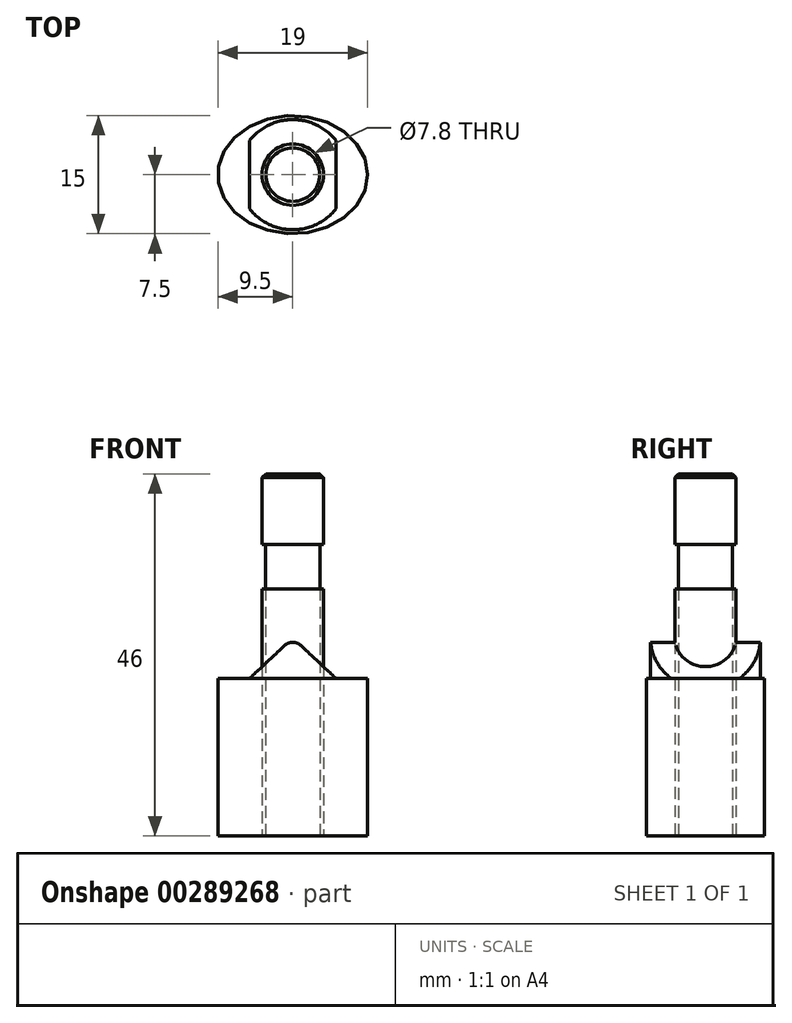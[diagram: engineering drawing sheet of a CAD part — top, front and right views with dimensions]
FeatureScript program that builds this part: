
annotation { "Feature Type Name" : "Feature", "Feature Type Description" : "" }
export const myFeature = defineFeature(function(context is Context, id is Id, definition is map)
    precondition{}
    {
        {
            var Q0;
            Q0=qCreatedBy(makeId("Top.planeOp"),FACE);
            var sketch = newSketch(context, id + "F0", { "sketchPlane" : qUnion([Q0])});
            skEllipse(sketch, "E0", {"center": v(0, 0) * mm, "majorRadius": 9.5 * mm, "minorRadius": 7.5 * mm, "majorAxis": v(1, 0)});
            skSolve(sketch);
        }
        {
            var Q0;
            Q0=makeQuery(id+"F0.imprint","IMPRINT",FACE,{"disambiguationData":[TD([[makeQuery(id+"F0.imprint","IMPRINT",EDGE,{"derivedFrom":sQuery(id+"F0.wireOp",EDGE,"E0")}),1.0]])]});
            extrude(context, id + "F1", {"entities" : qUnion([Q0]), "depth" : 20 * mm});
        }
        {
            var Q0;
            Q0=makeQuery(id+"F1.opExtrude","CAP_FACE",FACE,{"disambiguationData":[OSD([sQuery(id+"F0.wireOp",EDGE,"E0")])],"isStart":false});
            var sketch = newSketch(context, id + "F2", { "sketchPlane" : qUnion([Q0])});
            skCircle(sketch, "E1", {"center": v(0, 0) * mm, "radius": 7 * mm});
            skSolve(sketch);
        }
        {
            var Q0;
            Q0=makeQuery(id+"F2.imprint","IMPRINT",FACE,{"disambiguationData":[TD([[makeQuery(id+"F2.imprint","IMPRINT",EDGE,{"derivedFrom":sQuery(id+"F2.wireOp",EDGE,"E1")}),1.0]])]});
            extrude(context, id + "F3", {"entities" : qUnion([Q0]), "operationType" : NewBodyOperationType.ADD, "depth" : 4.6 * mm});
        }
        {
            var Q0;
            Q0=qCreatedBy(makeId("Front.planeOp"),FACE);
            var sketch = newSketch(context, id + "F4", { "sketchPlane" : qUnion([Q0])});
            skLineSegment(sketch, "E2.top", {"start": v(0, 24.6) * mm, "end": v(0, 24.6) * mm});
            skLineSegment(sketch, "E3", {"start": v(-5.5, 20) * mm, "end": v(-1.03, 24.2) * mm});
            skLineSegment(sketch, "E4", {"start": v(1.03, 24.2) * mm, "end": v(5.5, 20) * mm});
            skPoint(sketch, "E5.visualSharp", {"position": v(-0.6, 24.6) * mm});
            skArc(sketch, "E5.filletArc", {"start": v(0, 24.6) * mm, "mid": v(-0.55, 24.5) * mm, "end": v(-1.03, 24.2) * mm});
            skPoint(sketch, "E6.visualSharp", {"position": v(0.6, 24.6) * mm});
            skArc(sketch, "E6.filletArc", {"start": v(1.03, 24.2) * mm, "mid": v(0.55, 24.5) * mm, "end": v(0, 24.6) * mm});
            skLineSegment(sketch, "E7", {"start": v(-5.5, 20) * mm, "end": v(-7.13, 20) * mm});
            skLineSegment(sketch, "E8", {"start": v(-7.13, 20) * mm, "end": v(-7.13, 24.6) * mm});
            skLineSegment(sketch, "E9", {"start": v(-7.13, 24.6) * mm, "end": v(7.3, 24.6) * mm});
            skLineSegment(sketch, "E10", {"start": v(7.3, 24.6) * mm, "end": v(7.3, 20) * mm});
            skLineSegment(sketch, "E11", {"start": v(7.3, 20) * mm, "end": v(5.5, 20) * mm});
            skSolve(sketch);
        }
        {
            var Q0;
            Q0 = qSketchRegion(id + "F4", true);
            extrude(context, id + "F5", {"entities" : qUnion([Q0]), "operationType" : NewBodyOperationType.REMOVE, "endBound" : BoundingType.SYMMETRIC, "oppositeDirection" : true, "depth" : 25 * mm});
        }
        {
            var Q0;
            Q0=makeQuery(id+"F1.opExtrude","CAP_FACE",FACE,{"disambiguationData":[OSD([sQuery(id+"F0.wireOp",EDGE,"E0")])],"isStart":true});
            var sketch = newSketch(context, id + "F6", { "sketchPlane" : qUnion([Q0])});
            skCircle(sketch, "E12", {"center": v(0, 0) * mm, "radius": 3.9 * mm});
            skSolve(sketch);
        }
        {
            var Q0;
            Q0=makeQuery(id+"F6.imprint","IMPRINT",FACE,{"disambiguationData":[TD([[makeQuery(id+"F6.imprint","IMPRINT",EDGE,{"derivedFrom":sQuery(id+"F6.wireOp",EDGE,"E12")}),1.0]])]});
            extrude(context, id + "F7", {"entities" : qUnion([Q0]), "operationType" : NewBodyOperationType.REMOVE, "endBound" : BoundingType.THROUGH_ALL, "oppositeDirection" : true, "depth" : 25 * mm});
        }
        {
            var Q0;
            Q0=qCreatedBy(makeId("Top.planeOp"),FACE);
            var sketch = newSketch(context, id + "F8", { "sketchPlane" : qUnion([Q0])});
            skCircle(sketch, "E13", {"center": v(0, 0) * mm, "radius": 3.45 * mm});
            skSolve(sketch);
        }
        {
            var Q0;
            Q0 = qSketchRegion(id + "F8", true);
            extrude(context, id + "F9", {"entities" : qUnion([Q0]), "operationType" : NewBodyOperationType.ADD, "depth" : 46 * mm});
        }
        {
            var Q0;
            Q0=qCreatedBy(makeId("Top.planeOp"),FACE);
            var sketch = newSketch(context, id + "F10", { "sketchPlane" : qUnion([Q0])});
            skCircle(sketch, "E14", {"center": v(0, 0) * mm, "radius": 3.9 * mm});
            skSolve(sketch);
        }
        {
            var Q0;
            Q0 = qSketchRegion(id + "F10", true);
            extrude(context, id + "F11", {"entities" : qUnion([Q0]), "depth" : 31.4 * mm});
        }
        {
            var Q0;
            Q0=makeQuery(id+"F9.opExtrude","CAP_FACE",FACE,{"disambiguationData":[OSD([sQuery(id+"F8.wireOp",EDGE,"E13")])],"isStart":false});
            var sketch = newSketch(context, id + "F12", { "sketchPlane" : qUnion([Q0])});
            skCircle(sketch, "E15", {"center": v(0, 0) * mm, "radius": 3.9 * mm});
            skSolve(sketch);
        }
        {
            var Q0;
            Q0 = qSketchRegion(id + "F12", true);
            extrude(context, id + "F13", {"entities" : qUnion([Q0]), "operationType" : NewBodyOperationType.ADD, "oppositeDirection" : true, "depth" : 9 * mm});
        }
        {
            var Q0;
            Q0=makeQuery(id+"F13.opExtrude","CAP_EDGE",EDGE,{"disambiguationData":[OSD([sQuery(id+"F12.wireOp",EDGE,"E15")])],"isStart":true});
            chamfer(context, id + "F14", {"entities" : qUnion([Q0]), "width" : 0.5 * mm, "tangentPropagation" : true});
        }
    });
